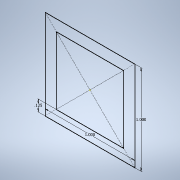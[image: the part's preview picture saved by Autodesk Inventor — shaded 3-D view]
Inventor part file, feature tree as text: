
AUTODESK INVENTOR PART (.ipt)
format: ipt  version: 2020.2 (Build 242310000, 310)  size: 90,624 bytes
history: native  units: in
note: dims shown in document units (in); Inventor stores cm internally (conversion verified against a paired STEP export)
features: sketch x1
ambient origin geometry x8: Origin, YZ Plane, XZ Plane, XY Plane, X Axis, Y Axis, Z Axis, Center Point
feature tree (1):
  sketch  "Sketch1"  dims[d0=1.0in d1=1.0in d2=0.125in]
